# Revit family: Gravity_Exhaust_Roof_Ventilators-GEGB_Carnes
name_source: partatom
category: Mechanical Equipment
revit_build: Autodesk Revit Architecture 2012 (Build: 20110309_2315(x64)
units: mm (PartAtom-declared; Revit-internal decimal feet)

## types (133) — shared parameters
04 CSI = 23 34 23
95 CSI = 15830
Assembly Code = D3040200
Catalog URL = http://www.carnes.com
Default Elevation = 0' - 0"
Description = Gravity Intake Roof Ventilator
Housing = Aluminum-Carnes-Spun-Brushed
Manufacturer = Carnes Company
Manufacturer Fax = 608-845-6470
Material = Aluminum or Steel
Model = GEGB
Product Page URL = http://www.carnes.com
Specifications URL = http://www.carnes.com
Subcategory = Ventilation
URL = http://www.carnes.com
Warranty URL = http://www.carnes.com

## per-type parameters (varying)
| type | Curb Cap Length | Curb Cap Width | G | Hood Length | Hood Width | Intake Throat Velocity 1000 | Intake Throat Velocity 1200 | Intake Throat Velocity 400 | Intake Throat Velocity 500 | Intake Throat Velocity 600 | Intake Throat Velocity 700 | Intake Throat Velocity 800 | Intake Throat Velocity 900 | Throat Area | Throat Size Length | Throat Size Width |
| 12x12 | 1' - 8" | 1' - 8" | 0' - 9" | 1' - 5" | 1' - 5" | 1000 | 1200 | 400 | 500 | 600 | 700 | 800 | 900 | 1.00 | 1' - 0" | 1' - 0" |
| 12x18 | 2' - 2" | 1' - 8" | 0' - 9" | 2' - 0" | 1' - 6" | 1500 | 1800 | 600 | 750 | 900 | 1050 | 1200 | 1350 | 1.50 | 1' - 6" | 1' - 0" |
| 12x24 | 2' - 8" | 1' - 8" | 0' - 9" | 2' - 7" | 1' - 7" | 2000 | 2400 | 800 | 1000 | 1200 | 1400 | 1600 | 1800 | 2.00 | 2' - 0" | 1' - 0" |
| 12x30 | 3' - 2" | 1' - 8" | 0' - 9" | 3' - 1" | 1' - 7" | 2500 | 3000 | 1000 | 1250 | 1500 | 1750 | 2000 | 2250 | 2.50 | 2' - 6" | 1' - 0" |
| 12x36 | 3' - 8" | 1' - 8" | 0' - 9" | 3' - 8" | 1' - 8" | 3000 | 3600 | 1200 | 1500 | 1800 | 2100 | 2400 | 2700 | 3.00 | 3' - 0" | 1' - 0" |
| 12x42 | 4' - 2" | 1' - 8" | 0' - 9" | 4' - 2" | 1' - 8" | 3500 | 4200 | 1400 | 1750 | 2100 | 2450 | 2800 | 3150 | 3.50 | 3' - 6" | 1' - 0" |
| 12x48 | 4' - 8" | 1' - 8" | 0' - 9" | 4' - 8" | 1' - 8" | 4000 | 4800 | 1600 | 2000 | 2400 | 2800 | 3200 | 3600 | 4.00 | 4' - 0" | 1' - 0" |
| 14x14 | 1' - 10" | 1' - 10" | 0' - 9" | 1' - 8" | 1' - 8" | 1361 | 1633 | 544 | 681 | 817 | 953 | 1089 | 1225 | 1.36 | 1' - 2" | 1' - 2" |
| 14x18 | 2' - 2" | 1' - 10" | 0' - 9" | 2' - 1" | 1' - 9" | 1750 | 2100 | 700 | 875 | 1050 | 1225 | 1400 | 1575 | 1.75 | 1' - 6" | 1' - 2" |
| 14x24 | 2' - 8" | 1' - 10" | 0' - 9" | 2' - 7" | 1' - 9" | 2333 | 2800 | 933 | 1167 | 1400 | 1633 | 1867 | 2100 | 2.33 | 2' - 0" | 1' - 2" |
| 14x30 | 3' - 2" | 1' - 10" | 0' - 9" | 3' - 3" | 1' - 11" | 2917 | 3500 | 1167 | 1458 | 1750 | 2042 | 2333 | 2625 | 2.92 | 2' - 6" | 1' - 2" |
| 14x36 | 3' - 8" | 1' - 10" | 0' - 9" | 3' - 9" | 1' - 11" | 3500 | 4200 | 1400 | 1750 | 2100 | 2450 | 2800 | 3150 | 3.50 | 3' - 0" | 1' - 2" |
| 14x42 | 4' - 2" | 1' - 10" | 0' - 9" | 4' - 3" | 1' - 11" | 4083 | 4900 | 1633 | 2042 | 2450 | 2858 | 3267 | 2675 | 4.08 | 3' - 6" | 1' - 2" |
| 14x48 | 4' - 8" | 1' - 10" | 0' - 9" | 4' - 9" | 1' - 11" | 4667 | 5600 | 1867 | 2333 | 2800 | 3267 | 3733 | 4200 | 4.67 | 4' - 0" | 1' - 2" |
| 16x16 | 2' - 0" | 2' - 0" | 0' - 10" | 1' - 11" | 1' - 11" | 1778 | 2133 | 711 | 889 | 1067 | 1244 | 1422 | 1600 | 1.78 | 1' - 4" | 1' - 4" |
| 16x18 | 2' - 2" | 2' - 0" | 0' - 10" | 2' - 1" | 1' - 11" | 2000 | 2400 | 800 | 1000 | 1200 | 1400 | 1600 | 1800 | 2.00 | 1' - 6" | 1' - 4" |
| 16x24 | 2' - 8" | 2' - 0" | 0' - 10" | 2' - 8" | 2' - 0" | 2667 | 3200 | 1067 | 1333 | 1600 | 1867 | 2133 | 2400 | 2.67 | 2' - 0" | 1' - 4" |
| 16x30 | 3' - 2" | 2' - 0" | 0' - 10" | 3' - 3" | 2' - 1" | 3333 | 4000 | 1333 | 1667 | 2000 | 2333 | 2667 | 3000 | 3.33 | 2' - 6" | 1' - 4" |
| 16x36 | 3' - 8" | 2' - 0" | 0' - 10" | 3' - 9" | 2' - 1" | 4000 | 4800 | 1600 | 2000 | 2400 | 2800 | 3200 | 3600 | 4.00 | 3' - 0" | 1' - 4" |
| 16x42 | 4' - 2" | 2' - 0" | 0' - 10" | 4' - 4" | 2' - 2" | 4667 | 5600 | 1867 | 2333 | 2800 | 3267 | 3733 | 4200 | 4.67 | 3' - 6" | 1' - 4" |
| 16x48 | 4' - 8" | 2' - 0" | 0' - 10" | 4' - 10" | 2' - 2" | 5333 | 6400 | 2133 | 2667 | 3200 | 3733 | 4267 | 4800 | 5.33 | 4' - 0" | 1' - 4" |
| 16x54 | 5' - 2" | 2' - 0" | 0' - 10" | 5' - 5" | 2' - 3" | 6000 | 7200 | 2400 | 3000 | 3600 | 4200 | 4800 | 5400 | 6.00 | 4' - 6" | 1' - 4" |
| 18x18 | 2' - 2" | 2' - 2" | 0' - 11" | 2' - 2" | 2' - 2" | 2250 | 2700 | 900 | 1125 | 1350 | 1575 | 1800 | 2025 | 2.25 | 1' - 6" | 1' - 6" |
| 18x20 | 2' - 4" | 2' - 2" | 0' - 11" | 2' - 4" | 2' - 2" | 2500 | 3000 | 1000 | 1250 | 1500 | 1750 | 2000 | 2250 | 2.50 | 1' - 8" | 1' - 6" |
| 18x24 | 2' - 8" | 2' - 2" | 0' - 11" | 2' - 9" | 2' - 3" | 3000 | 3600 | 1200 | 1500 | 1800 | 2100 | 2400 | 2700 | 3.00 | 2' - 0" | 1' - 6" |
| 18x30 | 3' - 2" | 2' - 2" | 0' - 11" | 3' - 3" | 2' - 3" | 3750 | 4500 | 1500 | 1875 | 2250 | 2625 | 3000 | 3375 | 3.75 | 2' - 6" | 1' - 6" |
| 18x36 | 3' - 8" | 2' - 2" | 0' - 11" | 3' - 11" | 2' - 5" | 4500 | 5400 | 1800 | 2250 | 2700 | 3150 | 3600 | 4050 | 4.50 | 3' - 0" | 1' - 6" |
| 18x42 | 4' - 2" | 2' - 2" | 0' - 11" | 4' - 5" | 2' - 5" | 5250 | 6300 | 2100 | 2625 | 3150 | 3675 | 4200 | 4725 | 5.25 | 3' - 6" | 1' - 6" |
| 18x48 | 4' - 8" | 2' - 2" | 0' - 11" | 4' - 11" | 2' - 5" | 6000 | 7200 | 2400 | 3000 | 3600 | 4200 | 4800 | 5400 | 6.00 | 4' - 0" | 1' - 6" |
| 18x54 | 5' - 2" | 2' - 2" | 0' - 11" | 5' - 6" | 2' - 6" | 6750 | 8100 | 2700 | 3375 | 4050 | 4725 | 5400 | 6075 | 6.75 | 4' - 6" | 1' - 6" |
| 18x60 | 5' - 8" | 2' - 2" | 0' - 11" | 6' - 0" | 2' - 6" | 7500 | 9000 | 3000 | 3750 | 4500 | 5250 | 6000 | 6750 | 7.50 | 5' - 0" | 1' - 6" |
| 20x20 | 2' - 4" | 2' - 4" | 1' - 0" | 2' - 5" | 2' - 5" | 2778 | 3333 | 1111 | 1389 | 1667 | 1944 | 2222 | 2500 | 2.78 | 1' - 8" | 1' - 8" |
| 20x22 | 2' - 6" | 2' - 4" | 1' - 0" | 2' - 7" | 2' - 5" | 3056 | 3667 | 1222 | 1528 | 1833 | 2139 | 2444 | 2750 | 3.06 | 1' - 10" | 1' - 8" |
| 20x24 | 2' - 8" | 2' - 4" | 1' - 0" | 2' - 9" | 2' - 5" | 3333 | 4000 | 1333 | 1667 | 2000 | 2333 | 2667 | 3000 | 3.33 | 2' - 0" | 1' - 8" |
| 20x30 | 3' - 2" | 2' - 4" | 1' - 0" | 3' - 5" | 2' - 7" | 4167 | 5000 | 1667 | 2083 | 2500 | 2917 | 3333 | 3750 | 4.17 | 2' - 6" | 1' - 8" |
| 20x36 | 3' - 8" | 2' - 4" | 1' - 0" | 3' - 11" | 2' - 7" | 5000 | 6000 | 2000 | 2500 | 3000 | 3500 | 4000 | 4500 | 5.00 | 3' - 0" | 1' - 8" |
| 20x42 | 4' - 2" | 2' - 4" | 1' - 0" | 4' - 5" | 2' - 7" | 5833 | 7000 | 2333 | 2917 | 3500 | 4083 | 4667 | 5250 | 5.83 | 3' - 6" | 1' - 8" |
| 20x48 | 4' - 8" | 2' - 4" | 1' - 0" | 5' - 0" | 2' - 8" | 6667 | 8000 | 2667 | 3333 | 4000 | 4667 | 5333 | 6000 | 6.67 | 4' - 0" | 1' - 8" |
| 20x54 | 5' - 2" | 2' - 4" | 1' - 0" | 5' - 6" | 2' - 8" | 7500 | 9000 | 3000 | 3750 | 4500 | 5250 | 6000 | 6750 | 7.50 | 4' - 6" | 1' - 8" |
| 20x60 | 5' - 8" | 2' - 4" | 1' - 0" | 6' - 1" | 2' - 9" | 8333 | 10000 | 3333 | 4167 | 5000 | 5833 | 6667 | 7500 | 8.33 | 5' - 0" | 1' - 8" |
| 20x66 | 6' - 2" | 2' - 4" | 1' - 0" | 6' - 7" | 2' - 9" | 9167 | 11000 | 3667 | 4583 | 5500 | 6417 | 7333 | 8250 | 9.17 | 5' - 6" | 1' - 8" |
| 20x72 | 6' - 8" | 2' - 4" | 1' - 0" | 7' - 2" | 2' - 10" | 10000 | 12000 | 4000 | 5000 | 6000 | 7000 | 8000 | 9000 | 10.00 | 6' - 0" | 1' - 8" |
| 20x84 | 7' - 8" | 2' - 4" | 1' - 0" | 8' - 2" | 2' - 10" | 11667 | 14000 | 4667 | 5833 | 7000 | 8167 | 9333 | 10500 | 11.67 | 7' - 0" | 1' - 8" |
| 22x22 | 2' - 6" | 2' - 6" | 1' - 0" | 2' - 8" | 2' - 8" | 3361 | 4033 | 1344 | 1681 | 2017 | 2353 | 2689 | 3025 | 3.36 | 1' - 10" | 1' - 10" |
| 22x24 | 2' - 8" | 2' - 6" | 1' - 0" | 2' - 10" | 2' - 8" | 3667 | 4400 | 1467 | 1833 | 2200 | 2567 | 2933 | 3300 | 3.67 | 2' - 0" | 1' - 10" |
| 22x30 | 3' - 2" | 2' - 6" | 1' - 0" | 3' - 5" | 2' - 9" | 4583 | 5500 | 1833 | 2292 | 2750 | 3208 | 3667 | 4125 | 4.58 | 2' - 6" | 1' - 10" |
| 22x36 | 3' - 8" | 2' - 6" | 1' - 0" | 3' - 11" | 2' - 9" | 5500 | 6600 | 2200 | 2750 | 3300 | 3850 | 4400 | 4950 | 5.50 | 3' - 0" | 1' - 10" |
| 22x42 | 4' - 2" | 2' - 6" | 1' - 0" | 4' - 7" | 2' - 11" | 6417 | 7700 | 2567 | 3208 | 3850 | 4492 | 5133 | 5775 | 6.43 | 3' - 6" | 1' - 10" |
| 22x48 | 4' - 8" | 2' - 6" | 1' - 0" | 5' - 1" | 2' - 11" | 7333 | 8800 | 2933 | 3667 | 4400 | 5133 | 5867 | 6600 | 7.33 | 4' - 0" | 1' - 10" |
| 22x54 | 5' - 2" | 2' - 6" | 1' - 0" | 5' - 7" | 2' - 11" | 8250 | 9900 | 3300 | 4125 | 4950 | 5775 | 6600 | 7425 | 8.25 | 4' - 6" | 1' - 10" |
| 22x60 | 5' - 8" | 2' - 6" | 1' - 0" | 6' - 2" | 3' - 0" | 9167 | 11000 | 3667 | 4583 | 5500 | 6417 | 7333 | 8250 | 9.17 | 5' - 0" | 1' - 10" |
| 22x66 | 6' - 2" | 2' - 6" | 1' - 0" | 6' - 8" | 3' - 0" | 10083 | 12100 | 4033 | 5042 | 6050 | 7058 | 8067 | 9075 | 10.08 | 5' - 6" | 1' - 10" |
| 22x72 | 6' - 8" | 2' - 6" | 1' - 0" | 7' - 3" | 3' - 1" | 11000 | 13200 | 4400 | 5500 | 6600 | 7700 | 8800 | 9900 | 11.00 | 6' - 0" | 1' - 10" |
| 22x84 | 7' - 8" | 2' - 6" | 1' - 0" | 8' - 3" | 3' - 1" | 12833 | 15400 | 5133 | 6417 | 7700 | 8983 | 10267 | 11550 | 12.83 | 7' - 0" | 1' - 10" |
| 24x24 | 2' - 8" | 2' - 8" | 1' - 1" | 2' - 11" | 2' - 11" | 4000 | 4800 | 1600 | 2000 | 2400 | 2800 | 3200 | 3600 | 4.00 | 2' - 0" | 2' - 0" |
| 24x30 | 3' - 2" | 2' - 8" | 1' - 1" | 3' - 5" | 2' - 11" | 5000 | 6000 | 2000 | 2500 | 3000 | 3500 | 4000 | 4500 | 5.00 | 2' - 6" | 2' - 0" |
| 24x36 | 3' - 8" | 2' - 8" | 1' - 1" | 3' - 4" | 3' - 1" | 6000 | 7200 | 2400 | 3000 | 3600 | 4200 | 4800 | 5400 | 6.00 | 3' - 0" | 2' - 0" |
| 24x42 | 4' - 2" | 2' - 8" | 1' - 1" | 4' - 7" | 3' - 1" | 7000 | 8400 | 2800 | 3500 | 4200 | 4900 | 5600 | 6300 | 7.00 | 3' - 6" | 2' - 0" |
| 24x48 | 4' - 8" | 2' - 8" | 1' - 1" | 5' - 1" | 3' - 1" | 8000 | 9600 | 3200 | 4000 | 4800 | 5600 | 6400 | 7200 | 8.00 | 4' - 0" | 2' - 0" |
| 24x54 | 5' - 2" | 2' - 8" | 1' - 1" | 5' - 9" | 3' - 3" | 9000 | 10800 | 3600 | 4500 | 5400 | 6300 | 7200 | 8100 | 9.00 | 4' - 6" | 2' - 0" |
| 24x60 | 5' - 8" | 2' - 8" | 1' - 1" | 6' - 3" | 3' - 3" | 10000 | 12000 | 4000 | 5000 | 6000 | 7000 | 8000 | 9000 | 10.00 | 5' - 0" | 2' - 0" |
| 24x66 | 6' - 2" | 2' - 8" | 1' - 1" | 6' - 9" | 3' - 3" | 11000 | 13200 | 4400 | 5500 | 6600 | 7700 | 8800 | 9900 | 11.00 | 5' - 6" | 2' - 0" |
| 24x72 | 6' - 8" | 2' - 8" | 1' - 1" | 7' - 3" | 3' - 3" | 12000 | 14400 | 4800 | 6000 | 7200 | 8400 | 9600 | 10800 | 12.00 | 6' - 0" | 2' - 0" |
| 24x84 | 7' - 8" | 2' - 8" | 1' - 1" | 8' - 4" | 3' - 4" | 14000 | 16800 | 5600 | 7000 | 8400 | 9800 | 11200 | 12600 | 14.00 | 7' - 0" | 2' - 0" |
| 24x96 | 8' - 8" | 2' - 8" | 1' - 1" | 9' - 5" | 3' - 5" | 16000 | 19200 | 6400 | 8000 | 9600 | 11200 | 12800 | 14400 | 16.00 | 8' - 0" | 2' - 0" |
| 30x30 | 3' - 2" | 3' - 2" | 1' - 3" | 3' - 6" | 3' - 6" | 6250 | 7500 | 2500 | 3125 | 3750 | 4375 | 5000 | 5625 | 6.25 | 2' - 6" | 2' - 6" |
| 30x36 | 3' - 8" | 3' - 2" | 1' - 3" | 4' - 3" | 3' - 9" | 7500 | 9000 | 3000 | 3750 | 4500 | 5250 | 6000 | 6750 | 7.50 | 3' - 0" | 2' - 6" |
| 30x42 | 4' - 2" | 3' - 2" | 1' - 3" | 4' - 9" | 3' - 9" | 8750 | 10500 | 3500 | 4375 | 5250 | 6125 | 7000 | 7875 | 8.75 | 3' - 6" | 2' - 6" |
| 30x48 | 4' - 8" | 3' - 2" | 1' - 3" | 5' - 3" | 3' - 9" | 10000 | 12000 | 4000 | 5000 | 6000 | 7000 | 8000 | 9000 | 10.00 | 4' - 0" | 2' - 6" |
| 30x54 | 5' - 2" | 3' - 2" | 1' - 3" | 5' - 11" | 3' - 11" | 11250 | 13500 | 4500 | 5625 | 6750 | 7875 | 9000 | 10125 | 11.25 | 4' - 6" | 2' - 6" |
| 30x60 | 5' - 8" | 3' - 2" | 1' - 3" | 6' - 5" | 3' - 11" | 12500 | 15000 | 5000 | 6250 | 7500 | 8750 | 10000 | 11250 | 12.50 | 5' - 0" | 2' - 6" |
| 30x66 | 6' - 2" | 3' - 2" | 1' - 3" | 6' - 11" | 3' - 11" | 13750 | 16500 | 5500 | 6875 | 8250 | 9625 | 11000 | 12375 | 13.75 | 5' - 6" | 2' - 6" |
| 30x72 | 6' - 8" | 3' - 2" | 1' - 3" | 7' - 7" | 4' - 1" | 15000 | 18000 | 6000 | 7500 | 9000 | 10500 | 12000 | 13500 | 15.00 | 6' - 0" | 2' - 6" |
| 30x84 | 7' - 8" | 3' - 2" | 1' - 3" | 8' - 7" | 4' - 1" | 17500 | 21000 | 7000 | 8750 | 10500 | 12250 | 14000 | 15750 | 17.50 | 7' - 0" | 2' - 6" |
| 30x96 | 8' - 8" | 3' - 2" | 1' - 3" | 9' - 8" | 4' - 2" | 20000 | 24000 | 8000 | 10000 | 12000 | 14000 | 16000 | 18000 | 20.00 | 8' - 0" | 2' - 6" |
| 30x108 | 9' - 8" | 3' - 2" | 1' - 3" | 10' - 8" | 4' - 2" | 22500 | 27000 | 9000 | 11250 | 13500 | 15750 | 18000 | 20250 | 22.50 | 9' - 0" | 2' - 6" |
| 30x120 | 10' - 8" | 3' - 2" | 1' - 3" | 11' - 9" | 4' - 3" | 25000 | 30000 | 10000 | 12500 | 15000 | 17500 | 20000 | 22500 | 25.00 | 10' - 0" | 2' - 6" |
| 36x36 | 3' - 8" | 3' - 8" | 1' - 5" | 4' - 4" | 4' - 4" | 9000 | 10800 | 3600 | 4500 | 5400 | 6300 | 7200 | 8100 | 9.00 | 3' - 0" | 3' - 0" |
| 36x42 | 4' - 2" | 3' - 8" | 1' - 5" | 4' - 10" | 4' - 4" | 10500 | 12600 | 4200 | 5250 | 6300 | 7350 | 8400 | 9450 | 10.50 | 3' - 6" | 3' - 0" |
| 36x48 | 4' - 8" | 3' - 8" | 1' - 5" | 5' - 6" | 4' - 6" | 12000 | 14400 | 4800 | 6000 | 7200 | 8400 | 9600 | 10800 | 12.00 | 4' - 0" | 3' - 0" |
| 36x54 | 5' - 2" | 3' - 8" | 1' - 5" | 6' - 0" | 4' - 6" | 13500 | 16200 | 5400 | 6750 | 8100 | 9450 | 10800 | 12150 | 13.50 | 4' - 6" | 3' - 0" |
| 36x60 | 5' - 8" | 3' - 8" | 1' - 5" | 6' - 8" | 4' - 8" | 15000 | 18000 | 6000 | 7500 | 9000 | 10500 | 12000 | 13500 | 15.00 | 5' - 0" | 3' - 0" |
| 36x66 | 6' - 2" | 3' - 8" | 1' - 5" | 8' - 0" | 4' - 8" | 16500 | 19800 | 6600 | 8250 | 9900 | 11550 | 13200 | 14850 | 16.50 | 5' - 6" | 3' - 0" |
| 36x72 | 6' - 8" | 3' - 8" | 1' - 5" | 8' - 1" | 4' - 8" | 18000 | 21600 | 7200 | 9000 | 10800 | 12600 | 14400 | 16200 | 18.00 | 6' - 0" | 3' - 0" |
| 36x84 | 7' - 8" | 3' - 8" | 1' - 5" | 8' - 9" | 4' - 9" | 21000 | 25200 | 8400 | 10500 | 12600 | 14700 | 16800 | 18900 | 21.00 | 7' - 0" | 3' - 0" |
| 36x96 | 8' - 8" | 3' - 8" | 1' - 5" | 9' - 10" | 4' - 10" | 24000 | 28800 | 9600 | 12000 | 14400 | 16800 | 19200 | 21600 | 24.00 | 8' - 0" | 3' - 0" |
| 36x108 | 9' - 8" | 3' - 8" | 1' - 5" | 10' - 11" | 4' - 11" | 27000 | 32400 | 10800 | 13500 | 16200 | 18900 | 21600 | 24300 | 27.00 | 9' - 0" | 3' - 0" |
| 36x120 | 10' - 8" | 3' - 8" | 1' - 5" | 12' - 0" | 5' - 0" | 30000 | 36000 | 12000 | 15000 | 18000 | 21000 | 24000 | 27000 | 30.00 | 10' - 0" | 3' - 0" |
| 42x42 | 4' - 2" | 4' - 2" | 1' - 7" | 4' - 10" | 4' - 10" | 12250 | 14700 | 4900 | 6125 | 7350 | 8575 | 9800 | 11025 | 12.25 | 3' - 6" | 3' - 6" |
| 42x48 | 4' - 8" | 4' - 2" | 1' - 7" | 5' - 7" | 5' - 1" | 14000 | 16800 | 5600 | 7000 | 8400 | 9800 | 11200 | 12600 | 14.00 | 4' - 0" | 3' - 6" |
| 42x54 | 5' - 2" | 4' - 2" | 1' - 7" | 6' - 1" | 5' - 1" | 15750 | 18900 | 6300 | 7875 | 9450 | 11025 | 12600 | 14175 | 15.75 | 4' - 6" | 3' - 6" |
| 42x60 | 5' - 8" | 4' - 2" | 1' - 7" | 7' - 3" | 5' - 3" | 17500 | 21000 | 7000 | 8750 | 10500 | 12250 | 14000 | 15750 | 17.50 | 5' - 0" | 3' - 6" |
| 42x66 | 6' - 2" | 4' - 2" | 1' - 7" | 7' - 3" | 5' - 3" | 19250 | 23100 | 7700 | 9625 | 11550 | 13475 | 15400 | 17325 | 19.25 | 5' - 6" | 3' - 6" |
| 42x72 | 6' - 8" | 4' - 2" | 1' - 7" | 7' - 9" | 5' - 3" | 21000 | 25200 | 8400 | 10500 | 12600 | 14700 | 16800 | 18900 | 21.00 | 6' - 0" | 3' - 6" |
| 42x84 | 7' - 8" | 4' - 2" | 1' - 7" | 8' - 11" | 5' - 5" | 24500 | 29400 | 9800 | 12250 | 14700 | 17150 | 19600 | 22050 | 24.5 | 7' - 0" | 3' - 6" |
| 42x96 | 8' - 8" | 4' - 2" | 1' - 7" | 10' - 0" | 5' - 6" | 28000 | 33600 | 11200 | 14000 | 16800 | 19600 | 22400 | 25200 | 28.00 | 8' - 0" | 3' - 6" |
| 42x108 | 9' - 8" | 4' - 2" | 1' - 7" | 11' - 1" | 5' - 7" | 31500 | 37800 | 12600 | 15750 | 18900 | 22050 | 25200 | 28350 | 31.50 | 9' - 0" | 3' - 6" |
| 42x120 | 10' - 8" | 4' - 2" | 1' - 7" | 12' - 4" | 5' - 8" | 35000 | 42000 | 14000 | 17500 | 21000 | 24500 | 28000 | 31500 | 35.00 | 10' - 0" | 3' - 6" |
| 48x48 | 4' - 8" | 4' - 8" | 1' - 9" | 5' - 9" | 5' - 9" | 16000 | 19200 | 6400 | 8000 | 9600 | 11200 | 12800 | 14400 | 16.00 | 4' - 0" | 4' - 0" |
| 48x54 | 5' - 2" | 4' - 8" | 1' - 9" | 6' - 3" | 5' - 9" | 18000 | 21600 | 7200 | 9000 | 10800 | 12600 | 14400 | 16200 | 18.00 | 4' - 6" | 4' - 0" |
| 48x60 | 5' - 8" | 4' - 8" | 1' - 9" | 6' - 11" | 5' - 11" | 20000 | 24000 | 8000 | 10000 | 12000 | 14000 | 16000 | 18000 | 20.00 | 5' - 0" | 4' - 0" |
| 48x66 | 6' - 2" | 4' - 8" | 1' - 9" | 7' - 5" | 5' - 11" | 22000 | 26400 | 8800 | 11000 | 13200 | 15400 | 17600 | 19800 | 22.00 | 5' - 6" | 4' - 0" |
| 48x72 | 6' - 8" | 4' - 8" | 1' - 9" | 7' - 11" | 5' - 11" | 24000 | 28800 | 9600 | 12000 | 14400 | 16800 | 19200 | 21600 | 24.00 | 6' - 0" | 4' - 0" |
| 48x84 | 7' - 8" | 4' - 8" | 1' - 9" | 9' - 1" | 6' - 1" | 28000 | 33600 | 11200 | 14000 | 16800 | 19600 | 22400 | 25200 | 18.00 | 7' - 0" | 4' - 0" |
| 48x96 | 8' - 8" | 4' - 8" | 1' - 9" | 10' - 3" | 6' - 3" | 32000 | 38400 | 12800 | 16000 | 19200 | 21400 | 25600 | 28800 | 32.00 | 8' - 0" | 4' - 0" |
| 48x108 | 9' - 8" | 4' - 8" | 1' - 9" | 11' - 4" | 6' - 4" | 36000 | 43200 | 14400 | 18000 | 21600 | 25200 | 28800 | 32400 | 36.00 | 9' - 0" | 4' - 0" |
| 48x120 | 10' - 8" | 4' - 8" | 1' - 9" | 12' - 5" | 6' - 5" | 40000 | 48000 | 16000 | 20000 | 24000 | 28000 | 32000 | 36000 | 40.00 | 10' - 0" | 4' - 0" |
| 54x54 | 5' - 2" | 5' - 2" | 1' - 11" | 6' - 4" | 6' - 4" | 20250 | 24300 | 8100 | 10125 | 12150 | 14175 | 16200 | 18225 | 20.25 | 4' - 6" | 4' - 6" |
| 54x60 | 5' - 8" | 5' - 2" | 1' - 11" | 7' - 1" | 6' - 7" | 22500 | 27000 | 9000 | 11250 | 13500 | 15750 | 18000 | 20250 | 22.50 | 5' - 0" | 4' - 6" |
| 54x66 | 6' - 2" | 5' - 2" | 1' - 11" | 7' - 7" | 6' - 7" | 24750 | 29700 | 9900 | 12375 | 14850 | 17325 | 19800 | 22275 | 24.75 | 5' - 6" | 4' - 6" |
| 54x72 | 6' - 8" | 5' - 2" | 1' - 11" | 8' - 2" | 6' - 8" | 27000 | 32400 | 10800 | 13500 | 16200 | 18900 | 21600 | 24300 | 27.00 | 6' - 0" | 4' - 6" |
| 54x84 | 7' - 8" | 5' - 2" | 1' - 11" | 9' - 3" | 6' - 9" | 31500 | 37800 | 12600 | 15750 | 18900 | 22050 | 25200 | 28350 | 31.50 | 7' - 0" | 4' - 6" |
| 54x96 | 8' - 8" | 5' - 2" | 1' - 11" | 10' - 5" | 6' - 11" | 36000 | 43200 | 14400 | 18000 | 21600 | 25200 | 28800 | 32400 | 36.00 | 8' - 0" | 4' - 6" |
| 54x108 | 9' - 8" | 5' - 2" | 1' - 11" | 11' - 6" | 7' - 0" | 40500 | 48600 | 16200 | 20250 | 24300 | 28350 | 32400 | 36450 | 40.50 | 9' - 0" | 4' - 6" |
| 54x120 | 10' - 8" | 5' - 2" | 1' - 11" | 12' - 7" | 7' - 1" | 45000 | 54000 | 18000 | 22500 | 27000 | 31500 | 36000 | 40500 | 45.00 | 10' - 0" | 4' - 6" |
| 60x60 | 5' - 8" | 5' - 8" | 2' - 1" | 7' - 2" | 7' - 2" | 25000 | 30000 | 10000 | 12500 | 15000 | 17500 | 20000 | 22500 | 25.00 | 5' - 0" | 5' - 0" |
| 60x66 | 6' - 2" | 5' - 8" | 2' - 1" | 7' - 8" | 7' - 2" | 27500 | 33000 | 11000 | 13750 | 16500 | 19250 | 22000 | 24750 | 27.50 | 5' - 6" | 5' - 0" |
| 60x72 | 6' - 8" | 5' - 8" | 2' - 1" | 8' - 3" | 7' - 3" | 30000 | 36000 | 12000 | 15000 | 18000 | 21000 | 24000 | 27000 | 30.00 | 6' - 0" | 5' - 0" |
| 60x84 | 7' - 8" | 5' - 8" | 2' - 1" | 9' - 5" | 7' - 5" | 35000 | 42000 | 14000 | 17500 | 21000 | 24500 | 28000 | 31500 | 35.00 | 7' - 0" | 5' - 0" |
| 60x90 | 8' - 8" | 5' - 8" | 2' - 1" | 10' - 6" | 7' - 6" | 40000 | 48000 | 16000 | 20000 | 24000 | 28000 | 32000 | 36000 | 40.00 | 7' - 6" | 5' - 0" |
| 60x108 | 9' - 8" | 5' - 8" | 2' - 1" | 11' - 8" | 7' - 8" | 45000 | 54000 | 18000 | 22500 | 27000 | 31500 | 36000 | 40500 | 45.00 | 9' - 0" | 5' - 0" |
| 60x120 | 10' - 8" | 5' - 8" | 2' - 1" | 12' - 9" | 7' - 9" | 50000 | 60000 | 20000 | 25000 | 30000 | 35000 | 40000 | 45000 | 50.00 | 10' - 0" | 5' - 0" |
| 66x66 | 6' - 2" | 6' - 2" | 2' - 2" | 7' - 9" | 7' - 9" | 30250 | 36300 | 12100 | 15125 | 18150 | 21175 | 24200 | 27225 | 30.25 | 5' - 6" | 5' - 6" |
| 66x72 | 6' - 8" | 6' - 2" | 2' - 2" | 8' - 5" | 7' - 11" | 33000 | 39600 | 13200 | 16500 | 19800 | 23100 | 26400 | 29700 | 33.00 | 6' - 0" | 5' - 6" |
| 66x84 | 7' - 8" | 6' - 2" | 2' - 2" | 9' - 7" | 8' - 1" | 38500 | 46200 | 15400 | 19250 | 23100 | 26950 | 30800 | 34650 | 38.50 | 7' - 0" | 5' - 6" |
| 66x96 | 8' - 8" | 6' - 2" | 2' - 2" | 10' - 8" | 8' - 2" | 44000 | 52800 | 17600 | 22000 | 26400 | 30800 | 35200 | 29600 | 44.00 | 8' - 0" | 5' - 6" |
| 66x108 | 9' - 8" | 6' - 2" | 2' - 2" | 11' - 10" | 8' - 4" | 49500 | 59400 | 19800 | 24750 | 29700 | 34650 | 39600 | 33550 | 49.50 | 9' - 0" | 5' - 6" |
| 66x120 | 10' - 8" | 6' - 2" | 2' - 2" | 12' - 11" | 8' - 5" | 55000 | 66000 | 22000 | 27500 | 33000 | 38500 | 44000 | 49500 | 55.00 | 10' - 0" | 5' - 6" |
| 72x72 | 6' - 8" | 6' - 8" | 2' - 4" | 8' - 6" | 8' - 6" | 36000 | 43200 | 14400 | 18000 | 21600 | 25200 | 28800 | 32400 | 36.00 | 6' - 0" | 6' - 0" |
| 72x84 | 7' - 8" | 6' - 8" | 2' - 4" | 9' - 8" | 8' - 8" | 42000 | 50400 | 16800 | 21000 | 25200 | 29400 | 33600 | 37800 | 42.00 | 7' - 0" | 6' - 0" |
| 72x96 | 8' - 8" | 6' - 8" | 2' - 4" | 10' - 10" | 8' - 10" | 48000 | 57600 | 19200 | 24000 | 28800 | 33600 | 38400 | 43200 | 48.00 | 8' - 0" | 6' - 0" |
| 72x108 | 9' - 8" | 6' - 8" | 2' - 4" | 12' - 0" | 9' - 0" | 54000 | 64800 | 21600 | 27000 | 32400 | 37800 | 43200 | 48600 | 54.00 | 9' - 0" | 6' - 0" |
| 72x120 | 10' - 8" | 6' - 8" | 2' - 4" | 13' - 2" | 9' - 2" | 60000 | 76200 | 24000 | 30000 | 36000 | 42000 | 48000 | 54000 | 60.00 | 10' - 0" | 6' - 0" |

## geometry (parser evidence)
native form markers: Blend x7, Sweep x1
no freeform markers — native parametric forms only
